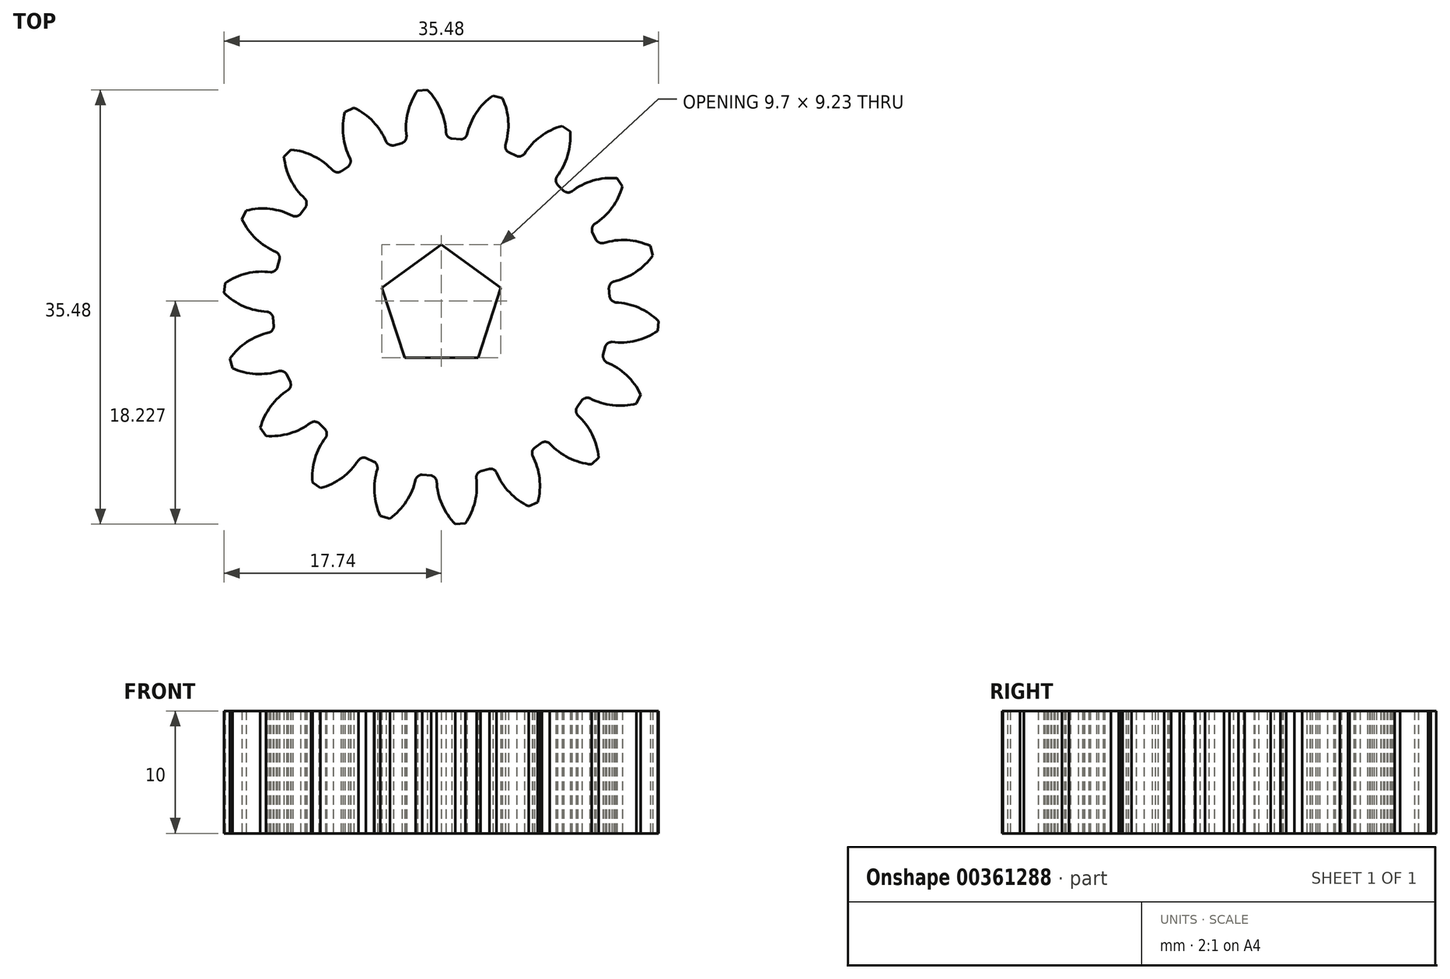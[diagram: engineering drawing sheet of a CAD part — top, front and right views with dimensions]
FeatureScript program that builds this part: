
annotation { "Feature Type Name" : "Feature", "Feature Type Description" : "" }
export const myFeature = defineFeature(function(context is Context, id is Id, definition is map)
    precondition{}
    {
        {
            var Q0;
            Q0=qCreatedBy(makeId("Top.planeOp"),FACE);
            var sketch = newSketch(context, id + "F0", { "sketchPlane" : qUnion([Q0])});
            skPoint(sketch, "E0.center", {"position": v(0, 0) * mm});
            skLineSegment(sketch, "E1", {"start": v(0, 0) * mm, "end": v(-5.13, -5.13) * mm, "construction": true});
            skCircle(sketch, "E2", {"center": v(0, 0) * mm, "radius": 1 * mm});
            skCircle(sketch, "E3", {"center": v(0, 0) * mm, "radius": 16 * mm, "construction": true});
            skCircle(sketch, "E4", {"center": v(0, 0) * mm, "radius": 13.78 * mm, "construction": true});
            skCircle(sketch, "E5", {"center": v(0, 0) * mm, "radius": 17.78 * mm, "construction": true});
            skCircle(sketch, "E6", {"center": v(0, 0) * mm, "radius": 17 * mm, "construction": true});
            skCircle(sketch, "E7", {"center": v(0, 0) * mm, "radius": 15.05 * mm, "construction": true});
            skLineSegment(sketch, "E8", {"start": v(0, 0) * mm, "end": v(-3.73, 14.64) * mm, "construction": true});
            skLineSegment(sketch, "E9", {"start": v(-3.73, 14.64) * mm, "end": v(-2.95, 12.49) * mm, "construction": true});
            skLineSegment(sketch, "E10", {"start": v(-0.18, 16.5) * mm, "end": v(0.18, 15.5) * mm, "construction": true});
            skLineSegment(sketch, "E11", {"start": v(-6.25, 13.73) * mm, "end": v(0, 0) * mm, "construction": true});
            skLineSegment(sketch, "E12", {"start": v(-6.25, 13.73) * mm, "end": v(-3.81, 10.36) * mm, "construction": true});
            skLineSegment(sketch, "E13", {"start": v(0, 0) * mm, "end": v(0.18, 15.5) * mm, "construction": true});
            skLineSegment(sketch, "E14", {"start": v(0.18, 15.5) * mm, "end": v(0.99, 11.26) * mm, "construction": true});
            skLineSegment(sketch, "E15", {"start": v(0.36, 14.58) * mm, "end": v(0, 0) * mm, "construction": true});
            skLineSegment(sketch, "E16", {"start": v(0.36, 14.58) * mm, "end": v(0.61, 11.2) * mm, "construction": true});
            skLineSegment(sketch, "E17", {"start": v(0, 0) * mm, "end": v(4.85, 17.75) * mm, "construction": true});
            skLineSegment(sketch, "E18", {"start": v(0, 0) * mm, "end": v(-0.18, 16.5) * mm, "construction": true});
            skLineSegment(sketch, "E19", {"start": v(-0.18, 16.5) * mm, "end": v(-2.53, 19.74) * mm, "construction": true});
            skLineSegment(sketch, "E20", {"start": v(-0.18, 16.5) * mm, "end": v(-0.8, 17.37) * mm, "construction": true});
            skArc(sketch, "E21.trimOffspring", {"start": v(-5.42, 14.04) * mm, "mid": v(-5.42, 14.03) * mm, "end": v(-5.42, 14.03) * mm});
            skCircle(sketch, "E22", {"center": v(0, 16) * mm, "radius": 1.4 * mm, "construction": true});
            skLineSegment(sketch, "E23", {"start": v(-1.4, 15.94) * mm, "end": v(0, 0) * mm, "construction": true});
            skArc(sketch, "E24.trimOffspring", {"start": v(0.38, 13.77) * mm, "mid": v(0.03, 15.92) * mm, "end": v(-1.15, 17.74) * mm});
            skArc(sketch, "E25.MirrorCS", {"start": v(-2.77, 13.5) * mm, "mid": v(-2.8, 15.67) * mm, "end": v(-1.95, 17.67) * mm});
            skLineSegment(sketch, "E26", {"start": v(-1.95, 17.67) * mm, "end": v(-1.15, 17.74) * mm});
            skLineSegment(sketch, "E27.1.0", {"start": v(-7.88, 15.94) * mm, "end": v(-7.15, 16.28) * mm});
            skArc(sketch, "E27.1.1", {"start": v(-4.35, 13.08) * mm, "mid": v(-5.41, 14.97) * mm, "end": v(-7.15, 16.28) * mm});
            skArc(sketch, "E27.1.2", {"start": v(-7.22, 11.74) * mm, "mid": v(-7.99, 13.77) * mm, "end": v(-7.88, 15.94) * mm});
            skLineSegment(sketch, "E27.2.0", {"start": v(-12.85, 12.28) * mm, "end": v(-12.28, 12.85) * mm});
            skArc(sketch, "E27.2.1", {"start": v(-8.56, 10.8) * mm, "mid": v(-10.2, 12.21) * mm, "end": v(-12.28, 12.85) * mm});
            skArc(sketch, "E27.2.2", {"start": v(-10.8, 8.56) * mm, "mid": v(-12.21, 10.2) * mm, "end": v(-12.85, 12.28) * mm});
            skLineSegment(sketch, "E27.3.0", {"start": v(-16.28, 7.15) * mm, "end": v(-15.94, 7.88) * mm});
            skArc(sketch, "E27.3.1", {"start": v(-11.74, 7.22) * mm, "mid": v(-13.77, 7.99) * mm, "end": v(-15.94, 7.88) * mm});
            skArc(sketch, "E27.3.2", {"start": v(-13.07, 4.35) * mm, "mid": v(-14.97, 5.42) * mm, "end": v(-16.28, 7.15) * mm});
            skLineSegment(sketch, "E27.4.0", {"start": v(-17.74, 1.15) * mm, "end": v(-17.67, 1.95) * mm});
            skArc(sketch, "E27.4.1", {"start": v(-13.5, 2.77) * mm, "mid": v(-15.67, 2.8) * mm, "end": v(-17.67, 1.95) * mm});
            skArc(sketch, "E27.4.2", {"start": v(-13.77, -0.38) * mm, "mid": v(-15.92, -0.03) * mm, "end": v(-17.74, 1.15) * mm});
            skLineSegment(sketch, "E27.5.0", {"start": v(-17.07, -4.99) * mm, "end": v(-17.27, -4.21) * mm});
            skArc(sketch, "E27.5.1", {"start": v(-13.63, -2.01) * mm, "mid": v(-15.68, -2.73) * mm, "end": v(-17.27, -4.21) * mm});
            skArc(sketch, "E27.5.2", {"start": v(-12.81, -5.07) * mm, "mid": v(-14.95, -5.47) * mm, "end": v(-17.07, -4.99) * mm});
            skLineSegment(sketch, "E27.6.0", {"start": v(-14.33, -10.53) * mm, "end": v(-14.8, -9.86) * mm});
            skArc(sketch, "E27.6.1", {"start": v(-12.12, -6.56) * mm, "mid": v(-13.8, -7.93) * mm, "end": v(-14.8, -9.86) * mm});
            skArc(sketch, "E27.6.2", {"start": v(-10.3, -9.15) * mm, "mid": v(-12.17, -10.26) * mm, "end": v(-14.33, -10.53) * mm});
            skLineSegment(sketch, "E27.7.0", {"start": v(-9.87, -14.8) * mm, "end": v(-10.53, -14.33) * mm});
            skArc(sketch, "E27.7.1", {"start": v(-9.15, -10.3) * mm, "mid": v(-10.26, -12.17) * mm, "end": v(-10.53, -14.33) * mm});
            skArc(sketch, "E27.7.2", {"start": v(-6.56, -12.12) * mm, "mid": v(-7.93, -13.8) * mm, "end": v(-9.87, -14.8) * mm});
            skLineSegment(sketch, "E27.8.0", {"start": v(-4.21, -17.27) * mm, "end": v(-5, -17.07) * mm});
            skArc(sketch, "E27.8.1", {"start": v(-5.07, -12.81) * mm, "mid": v(-5.47, -14.95) * mm, "end": v(-5, -17.07) * mm});
            skArc(sketch, "E27.8.2", {"start": v(-2.02, -13.63) * mm, "mid": v(-2.73, -15.68) * mm, "end": v(-4.21, -17.27) * mm});
            skLineSegment(sketch, "E27.9.0", {"start": v(1.95, -17.67) * mm, "end": v(1.15, -17.74) * mm});
            skArc(sketch, "E27.9.1", {"start": v(-0.38, -13.77) * mm, "mid": v(-0.03, -15.92) * mm, "end": v(1.15, -17.74) * mm});
            skArc(sketch, "E27.9.2", {"start": v(2.77, -13.5) * mm, "mid": v(2.8, -15.67) * mm, "end": v(1.95, -17.67) * mm});
            skLineSegment(sketch, "E27.10.0", {"start": v(7.88, -15.94) * mm, "end": v(7.15, -16.28) * mm});
            skArc(sketch, "E27.10.1", {"start": v(4.35, -13.08) * mm, "mid": v(5.41, -14.97) * mm, "end": v(7.15, -16.28) * mm});
            skArc(sketch, "E27.10.2", {"start": v(7.22, -11.74) * mm, "mid": v(7.99, -13.77) * mm, "end": v(7.88, -15.94) * mm});
            skLineSegment(sketch, "E27.11.0", {"start": v(12.85, -12.28) * mm, "end": v(12.28, -12.85) * mm});
            skArc(sketch, "E27.11.1", {"start": v(8.56, -10.8) * mm, "mid": v(10.2, -12.21) * mm, "end": v(12.28, -12.85) * mm});
            skArc(sketch, "E27.11.2", {"start": v(10.8, -8.56) * mm, "mid": v(12.21, -10.2) * mm, "end": v(12.85, -12.28) * mm});
            skLineSegment(sketch, "E27.12.0", {"start": v(16.28, -7.15) * mm, "end": v(15.94, -7.88) * mm});
            skArc(sketch, "E27.12.1", {"start": v(11.74, -7.22) * mm, "mid": v(13.77, -7.99) * mm, "end": v(15.94, -7.88) * mm});
            skArc(sketch, "E27.12.2", {"start": v(13.07, -4.35) * mm, "mid": v(14.97, -5.42) * mm, "end": v(16.28, -7.15) * mm});
            skLineSegment(sketch, "E27.13.0", {"start": v(17.74, -1.15) * mm, "end": v(17.67, -1.95) * mm});
            skArc(sketch, "E27.13.1", {"start": v(13.5, -2.77) * mm, "mid": v(15.67, -2.8) * mm, "end": v(17.67, -1.95) * mm});
            skArc(sketch, "E27.13.2", {"start": v(13.77, 0.38) * mm, "mid": v(15.92, 0.03) * mm, "end": v(17.74, -1.15) * mm});
            skLineSegment(sketch, "E27.14.0", {"start": v(17.07, 4.99) * mm, "end": v(17.27, 4.21) * mm});
            skArc(sketch, "E27.14.1", {"start": v(13.63, 2.01) * mm, "mid": v(15.68, 2.73) * mm, "end": v(17.27, 4.21) * mm});
            skArc(sketch, "E27.14.2", {"start": v(12.81, 5.07) * mm, "mid": v(14.95, 5.47) * mm, "end": v(17.07, 4.99) * mm});
            skLineSegment(sketch, "E27.15.0", {"start": v(14.33, 10.53) * mm, "end": v(14.8, 9.86) * mm});
            skArc(sketch, "E27.15.1", {"start": v(12.12, 6.56) * mm, "mid": v(13.8, 7.93) * mm, "end": v(14.8, 9.86) * mm});
            skArc(sketch, "E27.15.2", {"start": v(10.3, 9.15) * mm, "mid": v(12.17, 10.26) * mm, "end": v(14.33, 10.53) * mm});
            skLineSegment(sketch, "E27.16.0", {"start": v(9.87, 14.8) * mm, "end": v(10.53, 14.33) * mm});
            skArc(sketch, "E27.16.1", {"start": v(9.15, 10.3) * mm, "mid": v(10.26, 12.17) * mm, "end": v(10.53, 14.33) * mm});
            skArc(sketch, "E27.16.2", {"start": v(6.56, 12.12) * mm, "mid": v(7.93, 13.8) * mm, "end": v(9.87, 14.8) * mm});
            skLineSegment(sketch, "E27.17.0", {"start": v(4.21, 17.27) * mm, "end": v(5, 17.07) * mm});
            skArc(sketch, "E27.17.1", {"start": v(5.07, 12.81) * mm, "mid": v(5.47, 14.95) * mm, "end": v(5, 17.07) * mm});
            skArc(sketch, "E27.17.2", {"start": v(2.02, 13.63) * mm, "mid": v(2.73, 15.68) * mm, "end": v(4.21, 17.27) * mm});
            skCircle(sketch, "E28", {"center": v(0.38, 13.77) * mm, "radius": 0.45 * mm, "construction": true});
            skCircle(sketch, "E29", {"center": v(2.02, 13.63) * mm, "radius": 0.45 * mm, "construction": true});
            skArc(sketch, "E30", {"start": v(0.38, 14.22) * mm, "mid": v(0.54, 13.92) * mm, "end": v(0.83, 13.75) * mm});
            skArc(sketch, "E31", {"start": v(1.57, 13.7) * mm, "mid": v(1.89, 13.8) * mm, "end": v(2.1, 14.08) * mm});
            skLineSegment(sketch, "E32", {"start": v(0.83, 13.75) * mm, "end": v(1.57, 13.7) * mm});
            skArc(sketch, "E33.1.0", {"start": v(-4.5, 13.5) * mm, "mid": v(-4.25, 13.27) * mm, "end": v(-3.92, 13.21) * mm});
            skArc(sketch, "E33.1.1", {"start": v(-3.2, 13.4) * mm, "mid": v(-2.95, 13.62) * mm, "end": v(-2.85, 13.94) * mm});
            skLineSegment(sketch, "E33.1.2", {"start": v(-3.92, 13.21) * mm, "end": v(-3.2, 13.4) * mm});
            skArc(sketch, "E33.2.0", {"start": v(-8.85, 11.14) * mm, "mid": v(-8.54, 11.01) * mm, "end": v(-8.2, 11.07) * mm});
            skArc(sketch, "E33.2.1", {"start": v(-7.6, 11.5) * mm, "mid": v(-7.43, 11.79) * mm, "end": v(-7.44, 12.13) * mm});
            skLineSegment(sketch, "E33.2.2", {"start": v(-8.2, 11.07) * mm, "end": v(-7.6, 11.5) * mm});
            skArc(sketch, "E33.3.0", {"start": v(-12.13, 7.44) * mm, "mid": v(-11.79, 7.43) * mm, "end": v(-11.5, 7.6) * mm});
            skArc(sketch, "E33.3.1", {"start": v(-11.07, 8.2) * mm, "mid": v(-11.01, 8.54) * mm, "end": v(-11.14, 8.85) * mm});
            skLineSegment(sketch, "E33.3.2", {"start": v(-11.5, 7.6) * mm, "end": v(-11.07, 8.2) * mm});
            skArc(sketch, "E33.4.0", {"start": v(-13.94, 2.85) * mm, "mid": v(-13.62, 2.95) * mm, "end": v(-13.4, 3.21) * mm});
            skArc(sketch, "E33.4.1", {"start": v(-13.21, 3.92) * mm, "mid": v(-13.27, 4.26) * mm, "end": v(-13.5, 4.5) * mm});
            skLineSegment(sketch, "E33.4.2", {"start": v(-13.4, 3.21) * mm, "end": v(-13.21, 3.92) * mm});
            skArc(sketch, "E33.5.0", {"start": v(-14.07, -2.1) * mm, "mid": v(-13.8, -1.89) * mm, "end": v(-13.7, -1.57) * mm});
            skArc(sketch, "E33.5.1", {"start": v(-13.75, -0.83) * mm, "mid": v(-13.92, -0.54) * mm, "end": v(-14.23, -0.38) * mm});
            skLineSegment(sketch, "E33.5.2", {"start": v(-13.7, -1.57) * mm, "end": v(-13.75, -0.83) * mm});
            skArc(sketch, "E33.6.0", {"start": v(-12.51, -6.78) * mm, "mid": v(-12.33, -6.5) * mm, "end": v(-12.33, -6.15) * mm});
            skArc(sketch, "E33.6.1", {"start": v(-12.64, -5.49) * mm, "mid": v(-12.9, -5.27) * mm, "end": v(-13.24, -5.22) * mm});
            skLineSegment(sketch, "E33.6.2", {"start": v(-12.33, -6.15) * mm, "end": v(-12.64, -5.49) * mm});
            skArc(sketch, "E33.7.0", {"start": v(-9.44, -10.65) * mm, "mid": v(-9.36, -10.32) * mm, "end": v(-9.48, -10) * mm});
            skArc(sketch, "E33.7.1", {"start": v(-10, -9.48) * mm, "mid": v(-10.32, -9.36) * mm, "end": v(-10.65, -9.44) * mm});
            skLineSegment(sketch, "E33.7.2", {"start": v(-9.48, -10) * mm, "end": v(-10, -9.48) * mm});
            skArc(sketch, "E33.8.0", {"start": v(-5.23, -13.23) * mm, "mid": v(-5.27, -12.9) * mm, "end": v(-5.49, -12.64) * mm});
            skArc(sketch, "E33.8.1", {"start": v(-6.16, -12.33) * mm, "mid": v(-6.5, -12.33) * mm, "end": v(-6.78, -12.51) * mm});
            skLineSegment(sketch, "E33.8.2", {"start": v(-5.49, -12.64) * mm, "end": v(-6.16, -12.33) * mm});
            skArc(sketch, "E33.9.0", {"start": v(-0.38, -14.22) * mm, "mid": v(-0.54, -13.92) * mm, "end": v(-0.83, -13.75) * mm});
            skArc(sketch, "E33.9.1", {"start": v(-1.57, -13.7) * mm, "mid": v(-1.89, -13.8) * mm, "end": v(-2.1, -14.08) * mm});
            skLineSegment(sketch, "E33.9.2", {"start": v(-0.83, -13.75) * mm, "end": v(-1.57, -13.7) * mm});
            skArc(sketch, "E33.10.0", {"start": v(4.5, -13.5) * mm, "mid": v(4.25, -13.27) * mm, "end": v(3.92, -13.21) * mm});
            skArc(sketch, "E33.10.1", {"start": v(3.2, -13.4) * mm, "mid": v(2.95, -13.62) * mm, "end": v(2.85, -13.94) * mm});
            skLineSegment(sketch, "E33.10.2", {"start": v(3.92, -13.21) * mm, "end": v(3.2, -13.4) * mm});
            skArc(sketch, "E33.11.0", {"start": v(8.85, -11.14) * mm, "mid": v(8.54, -11.01) * mm, "end": v(8.2, -11.07) * mm});
            skArc(sketch, "E33.11.1", {"start": v(7.6, -11.5) * mm, "mid": v(7.43, -11.79) * mm, "end": v(7.44, -12.13) * mm});
            skLineSegment(sketch, "E33.11.2", {"start": v(8.2, -11.07) * mm, "end": v(7.6, -11.5) * mm});
            skArc(sketch, "E33.12.0", {"start": v(12.13, -7.44) * mm, "mid": v(11.79, -7.43) * mm, "end": v(11.5, -7.6) * mm});
            skArc(sketch, "E33.12.1", {"start": v(11.07, -8.2) * mm, "mid": v(11.01, -8.54) * mm, "end": v(11.14, -8.85) * mm});
            skLineSegment(sketch, "E33.12.2", {"start": v(11.5, -7.6) * mm, "end": v(11.07, -8.2) * mm});
            skArc(sketch, "E33.13.0", {"start": v(13.94, -2.85) * mm, "mid": v(13.62, -2.95) * mm, "end": v(13.4, -3.21) * mm});
            skArc(sketch, "E33.13.1", {"start": v(13.21, -3.92) * mm, "mid": v(13.27, -4.26) * mm, "end": v(13.5, -4.5) * mm});
            skLineSegment(sketch, "E33.13.2", {"start": v(13.4, -3.21) * mm, "end": v(13.21, -3.92) * mm});
            skArc(sketch, "E33.14.0", {"start": v(14.07, 2.1) * mm, "mid": v(13.8, 1.89) * mm, "end": v(13.7, 1.57) * mm});
            skArc(sketch, "E33.14.1", {"start": v(13.75, 0.83) * mm, "mid": v(13.92, 0.54) * mm, "end": v(14.23, 0.38) * mm});
            skLineSegment(sketch, "E33.14.2", {"start": v(13.7, 1.57) * mm, "end": v(13.75, 0.83) * mm});
            skArc(sketch, "E33.15.0", {"start": v(12.51, 6.78) * mm, "mid": v(12.33, 6.5) * mm, "end": v(12.33, 6.15) * mm});
            skArc(sketch, "E33.15.1", {"start": v(12.64, 5.49) * mm, "mid": v(12.9, 5.27) * mm, "end": v(13.24, 5.22) * mm});
            skLineSegment(sketch, "E33.15.2", {"start": v(12.33, 6.15) * mm, "end": v(12.64, 5.49) * mm});
            skArc(sketch, "E33.16.0", {"start": v(9.44, 10.65) * mm, "mid": v(9.36, 10.32) * mm, "end": v(9.48, 10) * mm});
            skArc(sketch, "E33.16.1", {"start": v(10, 9.48) * mm, "mid": v(10.32, 9.36) * mm, "end": v(10.65, 9.44) * mm});
            skLineSegment(sketch, "E33.16.2", {"start": v(9.48, 10) * mm, "end": v(10, 9.48) * mm});
            skArc(sketch, "E33.17.0", {"start": v(5.23, 13.23) * mm, "mid": v(5.27, 12.9) * mm, "end": v(5.49, 12.64) * mm});
            skArc(sketch, "E33.17.1", {"start": v(6.16, 12.33) * mm, "mid": v(6.5, 12.33) * mm, "end": v(6.78, 12.51) * mm});
            skLineSegment(sketch, "E33.17.2", {"start": v(5.49, 12.64) * mm, "end": v(6.16, 12.33) * mm});
            skLineSegment(sketch, "E34", {"start": v(-9.42, 11.47) * mm, "end": v(0, 0) * mm, "construction": true});
            skCircle(sketch, "E35.cCircle", {"center": v(0, 0) * mm, "radius": 4.13 * mm, "construction": true});
            skLineSegment(sketch, "E35.0", {"start": v(4.85, 1.58) * mm, "end": v(3, -4.13) * mm});
            skLineSegment(sketch, "E35.1", {"start": v(3, -4.13) * mm, "end": v(-3, -4.13) * mm});
            skLineSegment(sketch, "E35.2", {"start": v(-3, -4.13) * mm, "end": v(-4.85, 1.58) * mm});
            skLineSegment(sketch, "E35.3", {"start": v(-4.85, 1.58) * mm, "end": v(0, 5.1) * mm});
            skLineSegment(sketch, "E35.4", {"start": v(0, 5.1) * mm, "end": v(4.85, 1.58) * mm});
            skSolve(sketch);
        }
        {
            var Q0;
            {var subQ56=sQuery(id+"F0.wireOp",EDGE,"E26");Q0=makeQuery(id+"F0.imprint","IMPRINT",FACE,{"disambiguationData":[TD([[makeQuery(id+"F0.imprint","IMPRINT",EDGE,{"derivedFrom":subQ56}),-1.0]])]});}
            extrude(context, id + "F1", {"entities" : qUnion([Q0]), "depth" : 10 * mm});
        }
    });
